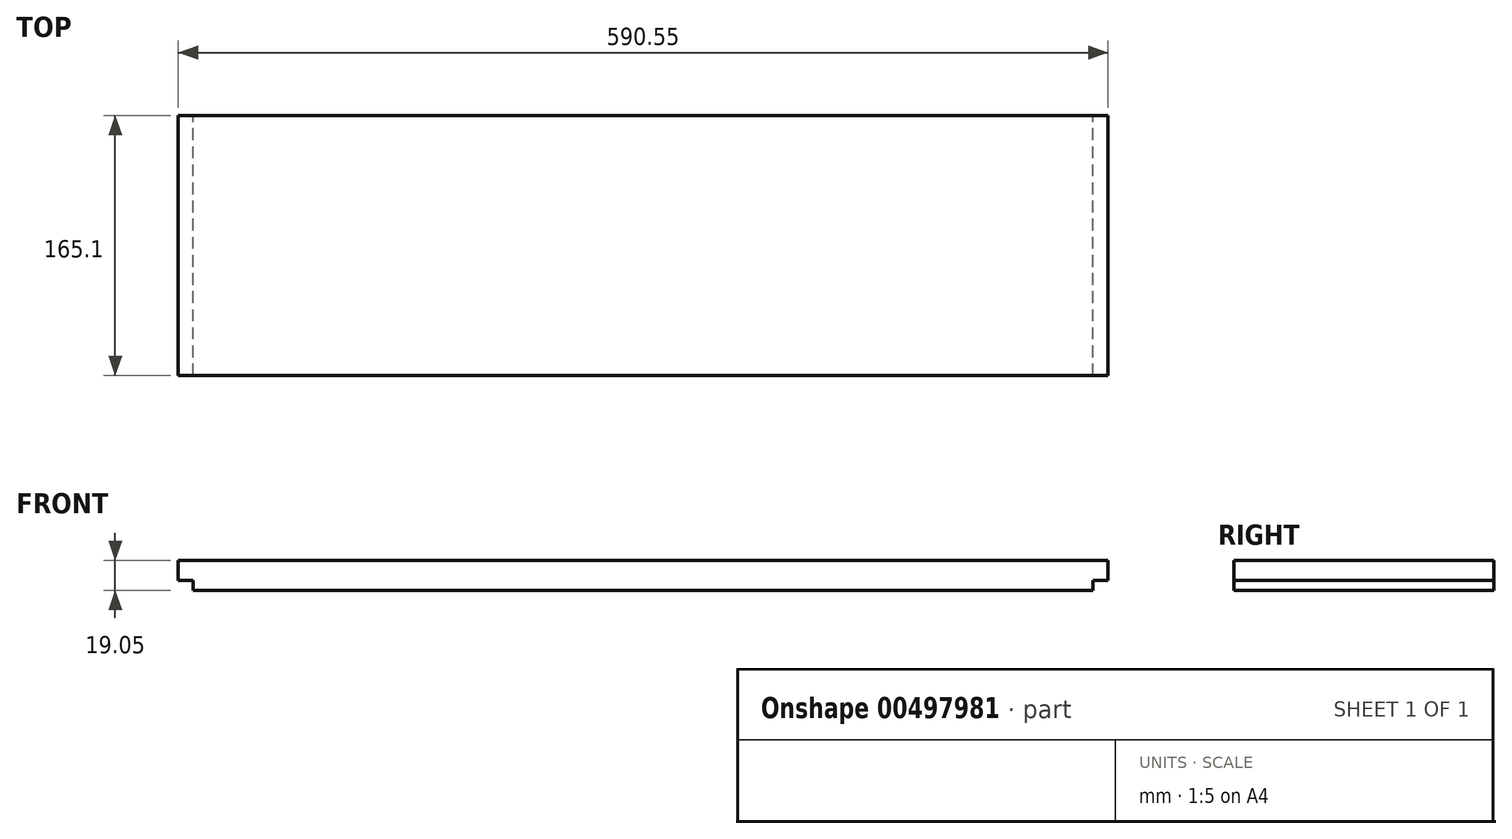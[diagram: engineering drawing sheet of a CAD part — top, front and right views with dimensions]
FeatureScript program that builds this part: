
annotation { "Feature Type Name" : "Feature", "Feature Type Description" : "" }
export const myFeature = defineFeature(function(context is Context, id is Id, definition is map)
    precondition{}
    {
        {
            var Q0;
            Q0=qCreatedBy(makeId("Right.planeOp"),FACE);
            var sketch = newSketch(context, id + "F0", { "sketchPlane" : qUnion([Q0])});
            skLineSegment(sketch, "E0.bottom", {"start": v(0, 0) * mm, "end": v(165.1, 0) * mm});
            skLineSegment(sketch, "E0.top", {"start": v(0, 19.05) * mm, "end": v(165.1, 19.05) * mm});
            skLineSegment(sketch, "E0.left", {"start": v(0, 0) * mm, "end": v(0, 19.05) * mm});
            skLineSegment(sketch, "E0.right", {"start": v(165.1, 0) * mm, "end": v(165.1, 19.05) * mm});
            skSolve(sketch);
        }
        {
            var Q0;
            Q0=makeQuery(id+"F0.imprint","IMPRINT",FACE,{"disambiguationData":[TD([[makeQuery(id+"F0.imprint","IMPRINT",EDGE,{"derivedFrom":sQuery(id+"F0.wireOp",EDGE,"E0.bottom")}),1.0]])]});
            extrude(context, id + "F1", {"entities" : qUnion([Q0]), "depth" : 590.55 * mm});
        }
        {
            var Q0;
            Q0=makeQuery(id+"F1.opExtrude","CAP_FACE",FACE,{"disambiguationData":[OSD([sQuery(id+"F0.wireOp",EDGE,"E0.bottom"),sQuery(id+"F0.wireOp",EDGE,"E0.top"),sQuery(id+"F0.wireOp",EDGE,"E0.left"),sQuery(id+"F0.wireOp",EDGE,"E0.right")])],"isStart":false});
            var sketch = newSketch(context, id + "F2", { "sketchPlane" : qUnion([Q0])});
            skLineSegment(sketch, "E1.0", {"start": v(0, 6.35) * mm, "end": v(165.1, 6.35) * mm});
            skSolve(sketch);
        }
        {
            var Q0;
            Q0 = qSketchRegion(id + "F2", true);
            var Q1;
            {var subQ0=sQuery(id+"F2.wireOp",EDGE,"E1.0");Q1=makeQuery(id+"F2.imprint","IMPRINT",FACE,{"disambiguationData":[TD([[makeQuery(id+"F2.imprint","IMPRINT",EDGE,{"derivedFrom":subQ0}),-1.0]])]});}
            extrude(context, id + "F3", {"entities" : qUnion([Q0, Q1]), "operationType" : NewBodyOperationType.REMOVE, "oppositeDirection" : true, "depth" : 9.52 * mm});
        }
        {
            var Q0;
            Q0=makeQuery(id+"F1.opExtrude","CAP_FACE",FACE,{"disambiguationData":[OSD([sQuery(id+"F0.wireOp",EDGE,"E0.bottom"),sQuery(id+"F0.wireOp",EDGE,"E0.top"),sQuery(id+"F0.wireOp",EDGE,"E0.left"),sQuery(id+"F0.wireOp",EDGE,"E0.right")])],"isStart":true});
            var sketch = newSketch(context, id + "F4", { "sketchPlane" : qUnion([Q0])});
            skLineSegment(sketch, "E2.0", {"start": v(0, 6.35) * mm, "end": v(-165.1, 6.35) * mm});
            skSolve(sketch);
        }
        {
            var Q0;
            Q0 = qSketchRegion(id + "F4", true);
            var Q1;
            {var subQ0=sQuery(id+"F4.wireOp",EDGE,"E2.0");Q1=makeQuery(id+"F4.imprint","IMPRINT",FACE,{"disambiguationData":[TD([[makeQuery(id+"F4.imprint","IMPRINT",EDGE,{"derivedFrom":subQ0}),1.0]])]});}
            extrude(context, id + "F5", {"entities" : qUnion([Q0, Q1]), "operationType" : NewBodyOperationType.REMOVE, "oppositeDirection" : true, "depth" : 9.52 * mm});
        }
    });
